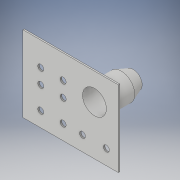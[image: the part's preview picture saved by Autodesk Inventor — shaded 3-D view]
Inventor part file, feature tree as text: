
AUTODESK INVENTOR PART (.ipt)
format: ipt  version: 2019 (Build 230136000, 136)  size: 148,480 bytes
history: native  units: mm
features: sketch x4, extrude x1, hole x1, revolve x1
ambient origin geometry x8: Origin, YZ Plane, XZ Plane, XY Plane, X Axis, Y Axis, Z Axis, Center Point
bodies: Solid1 (feature_tree)
feature tree (7):
  extrude  "Extrusion1"  Depth=51.0mm
  hole  "Hole1"  [1 undecoded]
  revolve  "Revolution1"  [1 undecoded]
  sketch  "Sketch8"  dims[d7=12.0mm d8=15.0mm d9=13.0mm d10=16.0mm d11=10.0mm d12=15.0mm d13=10.0mm d14=4.0mm d15=6.0mm d16=4.0mm d17=2.0mm d18=90.0deg d19=8.0mm d20=20.594885mm d33=25.0mm d34=1.0mm d35=5.0mm d36=90.0deg d37=17.0mm]
  sketch  "Sketch1"  dims[d0=64.0mm d1=51.0mm]
  sketch  "Sketch2"  dims[d2=18.0mm d3=16.0mm]
  sketch  "Sketch7"  dims[d4=16.0mm d5=1.0mm d6=0.0mm]
note: 2 required parameter values undecoded (feature->parameter linkage not recoverable at this tier; creation-order binding heuristic only, values carry confidence <= 0.55)